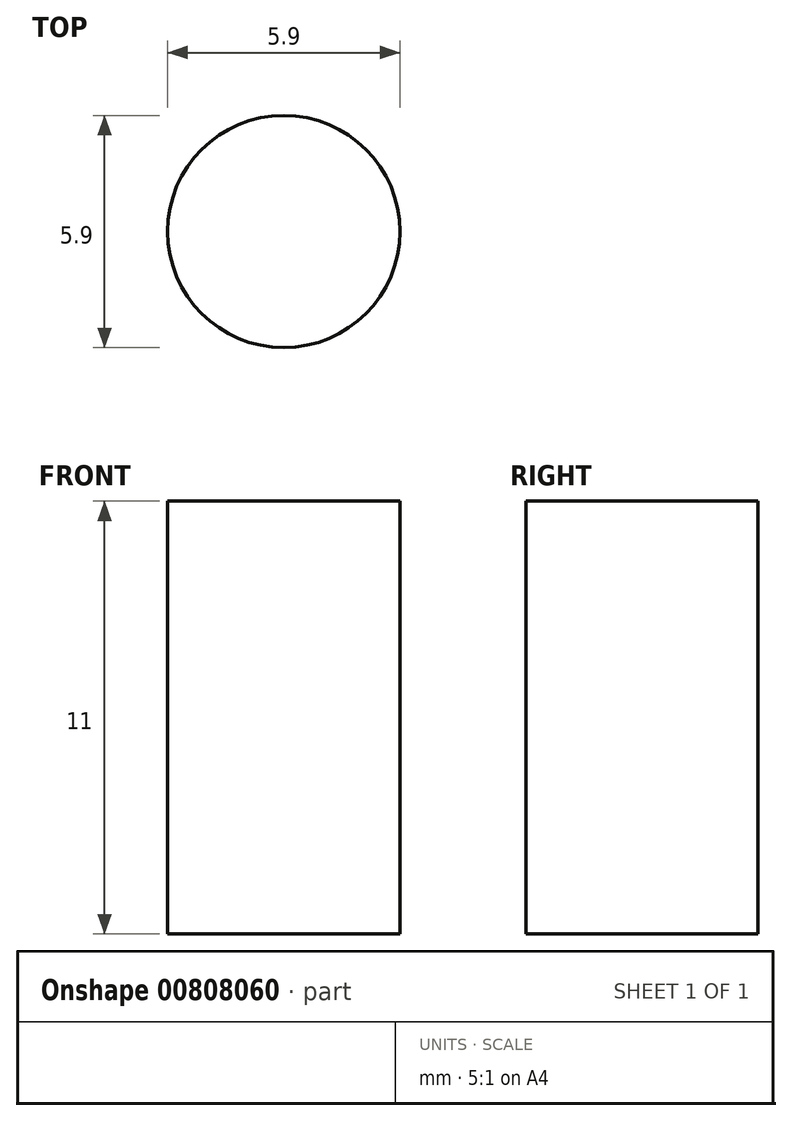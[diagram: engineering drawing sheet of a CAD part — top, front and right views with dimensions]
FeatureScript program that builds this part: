
annotation { "Feature Type Name" : "Feature", "Feature Type Description" : "" }
export const myFeature = defineFeature(function(context is Context, id is Id, definition is map)
    precondition{}
    {
        {
            var Q0;
            Q0=qCreatedBy(makeId("Top.planeOp"),FACE);
            var sketch = newSketch(context, id + "F0", { "sketchPlane" : qUnion([Q0])});
            skCircle(sketch, "E0", {"center": v(0, 0) * mm, "radius": 2.95 * mm});
            skSolve(sketch);
        }
        {
            var Q0;
            Q0=makeQuery(id+"F0.imprint","IMPRINT",FACE,{"disambiguationData":[TD([[makeQuery(id+"F0.imprint","IMPRINT",EDGE,{"derivedFrom":sQuery(id+"F0.wireOp",EDGE,"E0")}),1.0]])]});
            extrude(context, id + "F1", {"entities" : qUnion([Q0]), "depth" : 11 * mm, "offsetDistance" : 25 * mm});
        }
    });
